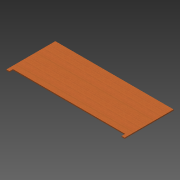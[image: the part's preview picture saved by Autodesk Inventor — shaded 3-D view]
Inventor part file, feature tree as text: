
AUTODESK INVENTOR PART (.ipt)
format: ipt  version: 2013 (Build 170138000, 138)  size: 83,456 bytes
history: native  units: in
note: dims shown in document units (in); Inventor stores cm internally (conversion verified against a paired STEP export)
features: extrude x1, sketch x1
ambient origin geometry x8: Origin, YZ Plane, XZ Plane, XY Plane, X Axis, Y Axis, Z Axis, Center Point
feature tree (2):
  extrude  "Extrusion2"  Depth=24.0in
  sketch  "Sketch1"  dims[d0=58.0in d1=24.0in d4=1.75in d8=0.5in d9=0.0in d10=1.5in d11=1.5in]
